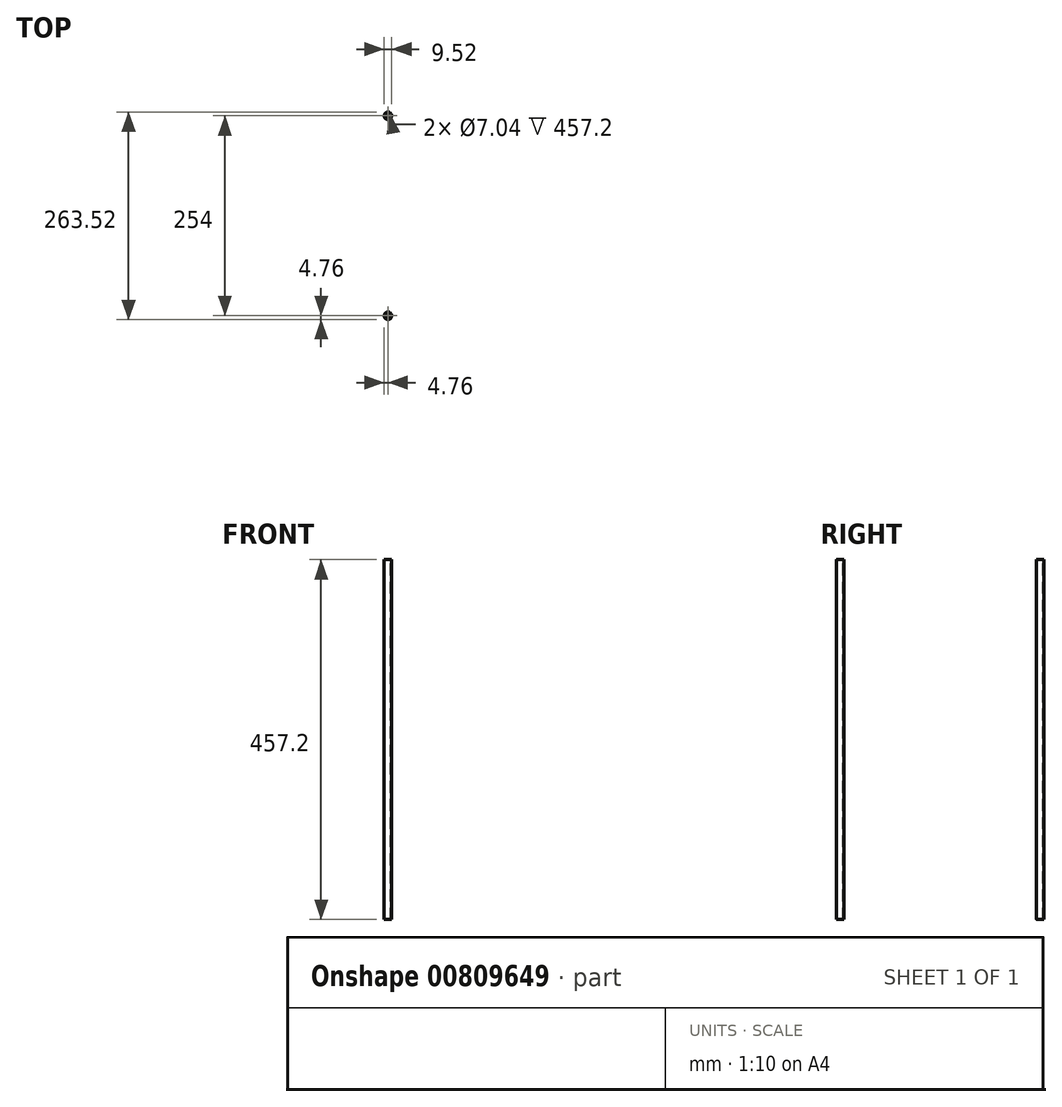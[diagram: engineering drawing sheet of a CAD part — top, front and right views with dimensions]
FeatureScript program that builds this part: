
annotation { "Feature Type Name" : "Feature", "Feature Type Description" : "" }
export const myFeature = defineFeature(function(context is Context, id is Id, definition is map)
    precondition{}
    {
        {
            var Q0;
            Q0=qCreatedBy(makeId("Top.planeOp"),FACE);
            var sketch = newSketch(context, id + "F0", { "sketchPlane" : qUnion([Q0])});
            skCircle(sketch, "E0", {"center": v(0, -127) * mm, "radius": 3.52 * mm});
            skCircle(sketch, "E1", {"center": v(0, -127) * mm, "radius": 4.76 * mm});
            skSolve(sketch);
        }
        {
            var Q0;
            Q0=makeQuery(id+"F0.imprint","IMPRINT",FACE,{"disambiguationData":[TD([[makeQuery(id+"F0.imprint","IMPRINT",EDGE,{"derivedFrom":sQuery(id+"F0.wireOp",EDGE,"E0")}),-1.0]])]});
            extrude(context, id + "F1", {"entities" : qUnion([Q0]), "oppositeDirection" : true, "depth" : 457.2 * mm, "offsetDistance" : 25.4 * mm});
        }
        {
            var Q0;
            Q0=makeQuery(id+"F1.opExtrude","SWEPT_BODY",BODY,{"disambiguationData":[OSD([sQuery(id+"F0.wireOp",EDGE,"E0"),sQuery(id+"F0.wireOp",EDGE,"E1")])]});
            var Q1;
            Q1=qCreatedBy(makeId("Front.planeOp"),FACE);
            mirror(context, id + "F2", {"entities" : qUnion([Q0]), "mirrorPlane" : qUnion([Q1])});
        }
    });
